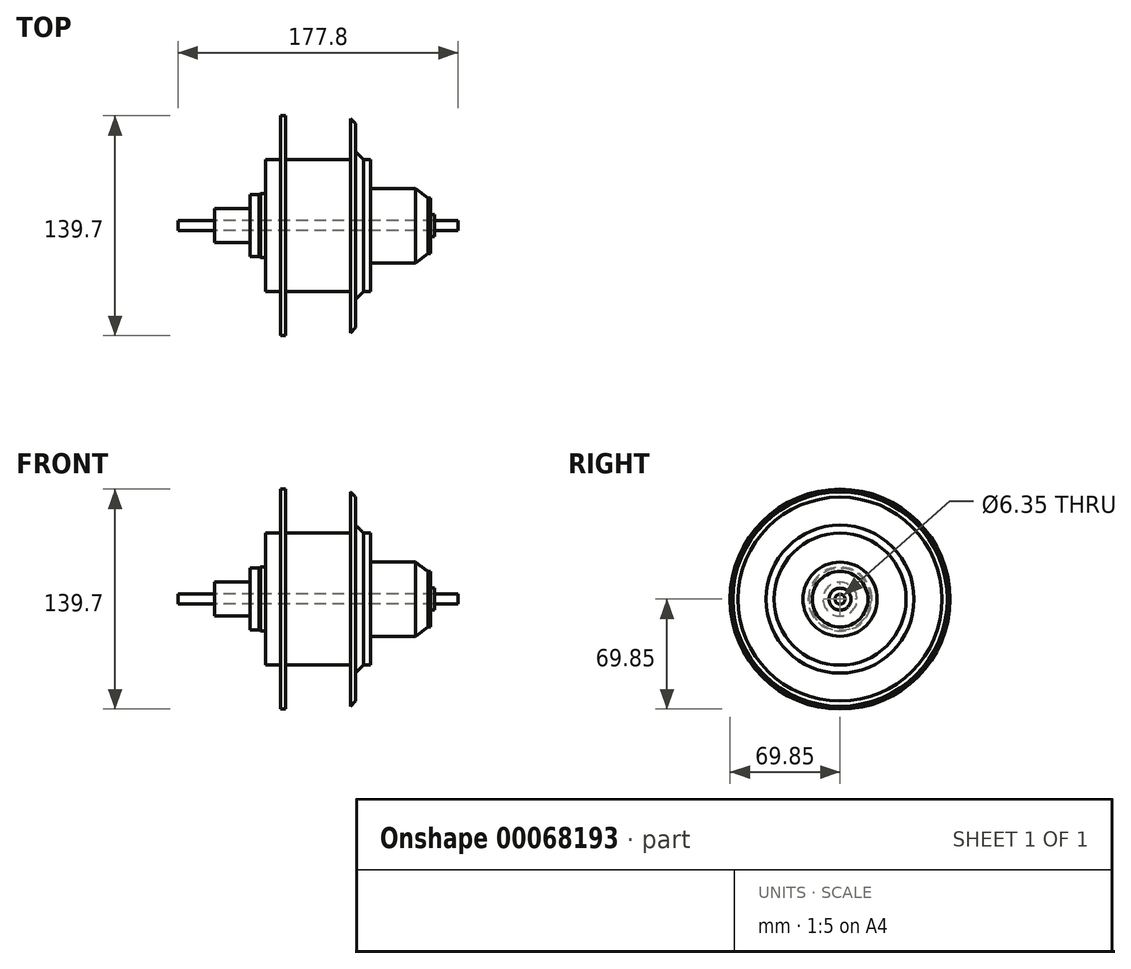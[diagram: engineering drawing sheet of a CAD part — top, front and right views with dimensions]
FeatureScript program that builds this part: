
annotation { "Feature Type Name" : "Feature", "Feature Type Description" : "" }
export const myFeature = defineFeature(function(context is Context, id is Id, definition is map)
    precondition{}
    {
        {
            var Q0;
            Q0=qCreatedBy(makeId("Right.planeOp"),FACE);
            var sketch = newSketch(context, id + "F0", { "sketchPlane" : qUnion([Q0])});
            skCircle(sketch, "E0", {"center": v(0, 0) * mm, "radius": 3.18 * mm});
            skSolve(sketch);
        }
        {
            var Q0;
            Q0=makeQuery(id+"F0.imprint","IMPRINT",FACE,{"disambiguationData":[TD([[makeQuery(id+"F0.imprint","IMPRINT",EDGE,{"derivedFrom":sQuery(id+"F0.wireOp",EDGE,"E0")}),1.0]])]});
            extrude(context, id + "F1", {"entities" : qUnion([Q0]), "endBound" : BoundingType.SYMMETRIC, "depth" : 177.8 * mm});
        }
        {
            var Q0;
            Q0=qCreatedBy(makeId("Front.planeOp"),FACE);
            var sketch = newSketch(context, id + "F2", { "sketchPlane" : qUnion([Q0])});
            skLineSegment(sketch, "E1", {"start": v(0, 0) * mm, "end": v(0, 41.9) * mm, "construction": true});
            skLineSegment(sketch, "E2.0", {"start": v(-88.9, 3.18) * mm, "end": v(-88.9, -3.18) * mm});
            skLineSegment(sketch, "E2.1", {"start": v(88.9, 3.18) * mm, "end": v(88.9, -3.18) * mm});
            skLineSegment(sketch, "E3", {"start": v(-65.57, 3.18) * mm, "end": v(74.13, 3.18) * mm});
            skLineSegment(sketch, "E4", {"start": v(74.13, 3.18) * mm, "end": v(74.13, 6.99) * mm});
            skLineSegment(sketch, "E5", {"start": v(74.13, 6.99) * mm, "end": v(71.55, 6.99) * mm});
            skLineSegment(sketch, "E6", {"start": v(71.55, 6.99) * mm, "end": v(71.55, 17.65) * mm});
            skLineSegment(sketch, "E7", {"start": v(71.55, 17.65) * mm, "end": v(69.83, 17.65) * mm});
            skLineSegment(sketch, "E8", {"start": v(69.83, 17.65) * mm, "end": v(61.84, 23.56) * mm});
            skLineSegment(sketch, "E9", {"start": v(61.84, 23.56) * mm, "end": v(33.2, 23.56) * mm});
            skLineSegment(sketch, "E10", {"start": v(33.2, 23.56) * mm, "end": v(33.2, 41.9) * mm});
            skLineSegment(sketch, "E11", {"start": v(33.2, 41.91) * mm, "end": v(23.92, 41.9) * mm});
            skLineSegment(sketch, "E12", {"start": v(23.92, 41.9) * mm, "end": v(23.92, 69.85) * mm});
            skLineSegment(sketch, "E13", {"start": v(23.92, 69.85) * mm, "end": v(20.62, 69.85) * mm});
            skLineSegment(sketch, "E14", {"start": v(20.62, 69.85) * mm, "end": v(20.62, 41.9) * mm});
            skLineSegment(sketch, "E15", {"start": v(20.62, 41.9) * mm, "end": v(-20.62, 41.9) * mm});
            skLineSegment(sketch, "E16", {"start": v(-20.62, 41.9) * mm, "end": v(-20.62, 69.85) * mm});
            skLineSegment(sketch, "E17", {"start": v(-20.62, 69.85) * mm, "end": v(-23.92, 69.85) * mm});
            skLineSegment(sketch, "E18", {"start": v(-23.92, 69.85) * mm, "end": v(-23.92, 41.9) * mm});
            skLineSegment(sketch, "E19", {"start": v(-23.92, 41.9) * mm, "end": v(-33.2, 41.9) * mm});
            skLineSegment(sketch, "E20", {"start": v(-33.2, 41.9) * mm, "end": v(-33.2, 20.32) * mm});
            skLineSegment(sketch, "E21", {"start": v(-33.2, 20.32) * mm, "end": v(-36.42, 20.32) * mm});
            skLineSegment(sketch, "E22", {"start": v(-36.42, 20.32) * mm, "end": v(-37.5, 19.68) * mm});
            skLineSegment(sketch, "E23", {"start": v(-37.5, 19.69) * mm, "end": v(-43.03, 19.69) * mm});
            skLineSegment(sketch, "E24", {"start": v(-43.03, 19.69) * mm, "end": v(-43.03, 10.79) * mm});
            skLineSegment(sketch, "E25", {"start": v(-43.03, 10.79) * mm, "end": v(-65.57, 10.79) * mm});
            skLineSegment(sketch, "E26", {"start": v(-65.57, 10.79) * mm, "end": v(-65.57, 3.18) * mm});
            skLineSegment(sketch, "E27", {"start": v(0, 0) * mm, "end": v(108.81, 0) * mm, "construction": true});
            skSolve(sketch);
        }
        {
            var Q0;
            Q0=makeQuery(id+"F2.imprint","IMPRINT",FACE,{"disambiguationData":[TD([[makeQuery(id+"F2.imprint","IMPRINT",EDGE,{"derivedFrom":sQuery(id+"F2.wireOp",EDGE,"E3")}),1.0]])]});
            var Q1;
            Q1=sQuery(id+"F2.wireOp",EDGE,"E27");
            revolve(context, id + "F3", {"entities" : qUnion([Q0]), "axis" : qUnion([Q1]), "revolveType" : RevolveType.FULL});
        }
        {
            var Q0;
            Q0=makeQuery(id+"F3.opRevolve","SWEPT_FACE",FACE,{"disambiguationData":[OSD([sQuery(id+"F2.wireOp",EDGE,"E6")])]});
            var sketch = newSketch(context, id + "F4", { "sketchPlane" : qUnion([Q0])});
            skSolve(sketch);
        }
        {
            var Q0;
            Q0=makeQuery(id+"F3.opRevolve","SWEPT_FACE",FACE,{"disambiguationData":[OSD([sQuery(id+"F2.wireOp",EDGE,"E12")])]});
            chamfer(context, id + "F5", {"entities" : qUnion([Q0]), "chamferType" : ChamferType.OFFSET_ANGLE, "width" : 5.08 * mm, "oppositeDirection" : false, "angle" : 45 * degree, "tangentPropagation" : true});
        }
    });
